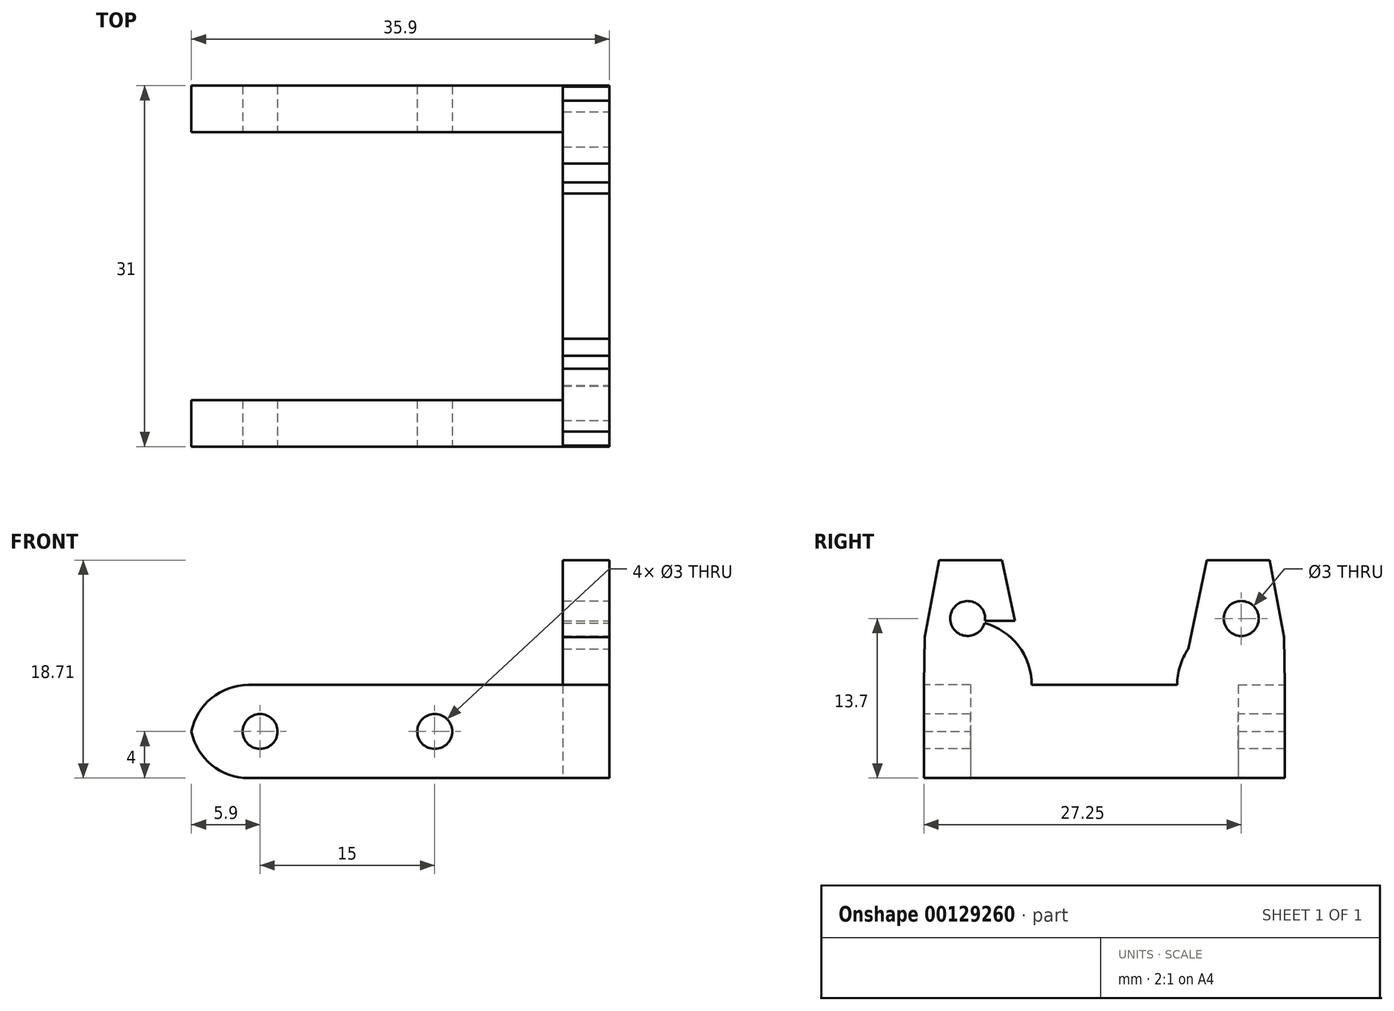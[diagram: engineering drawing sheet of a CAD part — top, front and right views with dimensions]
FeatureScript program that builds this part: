
annotation { "Feature Type Name" : "Feature", "Feature Type Description" : "" }
export const myFeature = defineFeature(function(context is Context, id is Id, definition is map)
    precondition{}
    {
        {
            var Q0;
            Q0=qCreatedBy(makeId("Top.planeOp"),FACE);
            var sketch = newSketch(context, id + "F0", { "sketchPlane" : qUnion([Q0])});
            skLineSegment(sketch, "E0", {"start": v(-25.25, 0) * mm, "end": v(21, 0) * mm, "construction": true});
            skLineSegment(sketch, "E1.0", {"start": v(-25.25, -11.5) * mm, "end": v(21, -11.5) * mm, "construction": true});
            skLineSegment(sketch, "E2", {"start": v(0, -19.54) * mm, "end": v(0, 24.09) * mm, "construction": true});
            skLineSegment(sketch, "E3.0", {"start": v(-18, -19.54) * mm, "end": v(-18, 24.09) * mm, "construction": true});
            skLineSegment(sketch, "E4.0", {"start": v(18, -19.54) * mm, "end": v(18, 24.09) * mm, "construction": true});
            skLineSegment(sketch, "E5.0", {"start": v(-12, -19.54) * mm, "end": v(-12, 24.09) * mm, "construction": true});
            skLineSegment(sketch, "E6.0", {"start": v(14, -19.54) * mm, "end": v(14, 24.09) * mm});
            skLineSegment(sketch, "E7", {"start": v(14, -11.5) * mm, "end": v(-18, -11.5) * mm});
            skLineSegment(sketch, "E8", {"start": v(-18, -11.5) * mm, "end": v(-18, -15.5) * mm});
            skLineSegment(sketch, "E9", {"start": v(-18, -15.5) * mm, "end": v(18, -15.5) * mm});
            skLineSegment(sketch, "E10", {"start": v(18, -15.5) * mm, "end": v(18, 0) * mm});
            skLineSegment(sketch, "E11.MirrorCS", {"start": v(-18, 15.5) * mm, "end": v(18, 15.5) * mm});
            skLineSegment(sketch, "E12.MirrorCS", {"start": v(14, 11.5) * mm, "end": v(-18, 11.5) * mm});
            skLineSegment(sketch, "E13.MirrorCS", {"start": v(-18, 11.5) * mm, "end": v(-18, 15.5) * mm});
            skLineSegment(sketch, "E14.MirrorCS", {"start": v(18, 15.5) * mm, "end": v(18, 0) * mm});
            skSolve(sketch);
        }
        {
            var Q0;
            {var subQ0=sQuery(id+"F0.wireOp",EDGE,"E12.MirrorCS");Q0=makeQuery(id+"F0.imprint","IMPRINT",FACE,{"disambiguationData":[TD([[makeQuery(id+"F0.imprint","IMPRINT",EDGE,{"derivedFrom":subQ0}),-1.0]])]});}
            var Q1;
            {var subQ0=sQuery(id+"F0.wireOp",EDGE,"E10");Q1=makeQuery(id+"F0.imprint","IMPRINT",FACE,{"disambiguationData":[TD([[makeQuery(id+"F0.imprint","IMPRINT",EDGE,{"derivedFrom":subQ0}),1.0]])]});}
            var Q2;
            {var subQ0=sQuery(id+"F0.wireOp",EDGE,"E7");Q2=makeQuery(id+"F0.imprint","IMPRINT",FACE,{"disambiguationData":[TD([[makeQuery(id+"F0.imprint","IMPRINT",EDGE,{"derivedFrom":subQ0}),1.0]])]});}
            extrude(context, id + "F1", {"entities" : qUnion([Q0, Q1, Q2]), "depth" : 8 * mm});
        }
        {
            var Q0;
            Q0=makeQuery(id+"F1.opExtrude","SWEPT_FACE",FACE,{"disambiguationData":[OSD([sQuery(id+"F0.wireOp",EDGE,"E10"),sQuery(id+"F0.wireOp",EDGE,"E14.MirrorCS")])]});
            var sketch = newSketch(context, id + "F2", { "sketchPlane" : qUnion([Q0])});
            skPoint(sketch, "E15.0", {"position": v(0, 0) * mm});
            skLineSegment(sketch, "E16.0", {"start": v(-15.5, 0) * mm, "end": v(15.5, 0) * mm, "construction": true});
            skLineSegment(sketch, "E17.0", {"start": v(-15.5, 8) * mm, "end": v(15.5, 8) * mm, "construction": true});
            skLineSegment(sketch, "E18", {"start": v(0, 0) * mm, "end": v(0, 8) * mm, "construction": true});
            skLineSegment(sketch, "E19.0", {"start": v(11.75, 0) * mm, "end": v(11.75, 8) * mm});
            skArc(sketch, "E20", {"start": v(15.42, 12.1) * mm, "mid": v(6.61, 9.97) * mm, "end": v(11.75, 2.5) * mm});
            skArc(sketch, "E21.MirrorC", {"start": v(-15.42, 12.1) * mm, "mid": v(-9.5, 13.02) * mm, "end": v(-6.25, 8) * mm});
            skLineSegment(sketch, "E22", {"start": v(11.75, 8) * mm, "end": v(11.75, 13.5) * mm, "construction": true});
            skLineSegment(sketch, "E23", {"start": v(11.75, 13.5) * mm, "end": v(-11.75, 13.5) * mm});
            skLineSegment(sketch, "E24.0", {"start": v(-13.75, 13.7) * mm, "end": v(13.75, 13.7) * mm, "construction": true});
            skCircle(sketch, "E25", {"center": v(11.75, 13.7) * mm, "radius": 1.5 * mm});
            skCircle(sketch, "E26.MirrorC", {"center": v(-11.75, 13.7) * mm, "radius": 1.5 * mm});
            skLineSegment(sketch, "E27", {"start": v(-15.42, 12.1) * mm, "end": v(-14.2, 18.71) * mm});
            skLineSegment(sketch, "E28", {"start": v(-14.2, 18.71) * mm, "end": v(-8.8, 18.71) * mm});
            skLineSegment(sketch, "E29", {"start": v(-8.8, 18.71) * mm, "end": v(-7.2, 11.09) * mm});
            skLineSegment(sketch, "E30.MirrorCS", {"start": v(8.8, 18.71) * mm, "end": v(7.2, 11.09) * mm});
            skLineSegment(sketch, "E31.MirrorCS", {"start": v(14.2, 18.71) * mm, "end": v(8.8, 18.71) * mm});
            skLineSegment(sketch, "E32.MirrorCS", {"start": v(15.42, 12.1) * mm, "end": v(14.2, 18.71) * mm});
            skLineSegment(sketch, "E33", {"start": v(-15.42, 12.1) * mm, "end": v(-15.5, 8) * mm});
            skLineSegment(sketch, "E34", {"start": v(15.42, 12.1) * mm, "end": v(15.5, 8) * mm});
            skSolve(sketch);
        }
        {
            var Q0;
            {var subQ0=sQuery(id+"F2.wireOp",EDGE,"E21.MirrorC");var subQ8=makeQuery(id+"F2.imprint","INTERSECT",VERTEX,{"derivedFrom":[subQ0,sQuery(id+"F2.wireOp",EDGE,"E27")]});Q0=makeQuery(id+"F2.imprint","IMPRINT",FACE,{"disambiguationData":[TD([[makeQuery(id+"F2.imprint","IMPRINT",EDGE,{"disambiguationData":[TD([[subQ8,-1.0]])],"derivedFrom":subQ0}),-1.0]])]});}
            var Q1;
            {var subQ0=sQuery(id+"F2.wireOp",EDGE,"E20");var subQ10=makeQuery(id+"F2.imprint","INTERSECT",VERTEX,{"derivedFrom":[subQ0,sQuery(id+"F2.wireOp",EDGE,"E32.MirrorCS")]});Q1=makeQuery(id+"F2.imprint","IMPRINT",FACE,{"disambiguationData":[TD([[makeQuery(id+"F2.imprint","IMPRINT",EDGE,{"disambiguationData":[TD([[subQ10,-1.0]])],"derivedFrom":subQ0}),1.0]])]});}
            var Q2;
            {var subQ8=sQuery(id+"F2.wireOp",EDGE,"E27");Q2=makeQuery(id+"F2.imprint","IMPRINT",FACE,{"disambiguationData":[TD([[makeQuery(id+"F2.imprint","IMPRINT",EDGE,{"derivedFrom":subQ8}),-1.0]])]});}
            var Q3;
            {var subQ0=sQuery(id+"F2.wireOp",EDGE,"E29");var subQ1=sQuery(id+"F2.wireOp",EDGE,"E21.MirrorC");var subQ2=makeQuery(id+"F2.imprint","INTERSECT",VERTEX,{"derivedFrom":[subQ1,subQ0]});Q3=makeQuery(id+"F2.imprint","IMPRINT",FACE,{"disambiguationData":[TD([[makeQuery(id+"F2.imprint","IMPRINT",EDGE,{"disambiguationData":[TD([[subQ2,1.0]])],"derivedFrom":subQ1}),1.0]])]});}
            var Q4;
            {var subQ0=sQuery(id+"F2.wireOp",EDGE,"E31.MirrorCS");Q4=makeQuery(id+"F2.imprint","IMPRINT",FACE,{"disambiguationData":[TD([[makeQuery(id+"F2.imprint","IMPRINT",EDGE,{"derivedFrom":subQ0}),1.0]])]});}
            var Q5;
            {var subQ0=sQuery(id+"F2.wireOp",EDGE,"E30.MirrorCS");var subQ1=sQuery(id+"F2.wireOp",EDGE,"E20");var subQ2=makeQuery(id+"F2.imprint","INTERSECT",VERTEX,{"derivedFrom":[subQ1,subQ0]});Q5=makeQuery(id+"F2.imprint","IMPRINT",FACE,{"disambiguationData":[TD([[makeQuery(id+"F2.imprint","IMPRINT",EDGE,{"disambiguationData":[TD([[subQ2,1.0]])],"derivedFrom":subQ1}),-1.0]])]});}
            var Q6;
            Q6=makeQuery(id+"F1.opExtrude","SWEPT_FACE",FACE,{"disambiguationData":[OSD([sQuery(id+"F0.wireOp",EDGE,"E6.0")])]});
            extrude(context, id + "F3", {"entities" : qUnion([Q0, Q1, Q2, Q3, Q4, Q5]), "operationType" : NewBodyOperationType.ADD, "endBound" : BoundingType.UP_TO_SURFACE, "oppositeDirection" : true, "endBoundEntityFace" : qUnion([Q6]), "depth" : 25 * mm});
        }
        {
            var Q0;
            Q0=makeQuery(id+"F2.imprint","IMPRINT",FACE,{"disambiguationData":[TD([[makeQuery(id+"F2.imprint","IMPRINT",EDGE,{"derivedFrom":sQuery(id+"F2.wireOp",EDGE,"E25")}),1.0]])]});
            var Q1;
            Q1=makeQuery(id+"F2.imprint","IMPRINT",FACE,{"disambiguationData":[TD([[makeQuery(id+"F2.imprint","IMPRINT",EDGE,{"derivedFrom":sQuery(id+"F2.wireOp",EDGE,"E26.MirrorC")}),-1.0]])]});
            extrude(context, id + "F4", {"entities" : qUnion([Q0, Q1]), "operationType" : NewBodyOperationType.REMOVE, "oppositeDirection" : true, "depth" : 25 * mm});
        }
        {
            var Q0;
            Q0=makeQuery(id+"F1.opExtrude","SWEPT_FACE",FACE,{"disambiguationData":[OSD([sQuery(id+"F0.wireOp",EDGE,"E9")])]});
            var sketch = newSketch(context, id + "F5", { "sketchPlane" : qUnion([Q0])});
            skLineSegment(sketch, "E35.0.0", {"start": v(14, 8) * mm, "end": v(14, 8) * mm});
            skLineSegment(sketch, "E35.0.1", {"start": v(14, 8) * mm, "end": v(14, 8) * mm});
            skLineSegment(sketch, "E35.0.2", {"start": v(-18, 8) * mm, "end": v(-18, 0) * mm});
            skLineSegment(sketch, "E35.0.3", {"start": v(-18, 0) * mm, "end": v(18, 0) * mm});
            skLineSegment(sketch, "E35.0.4", {"start": v(18, 0) * mm, "end": v(18, 8) * mm});
            skLineSegment(sketch, "E35.0.5", {"start": v(18, 8) * mm, "end": v(14, 8) * mm});
            skPoint(sketch, "E36.0", {"position": v(-12, 0) * mm});
            skLineSegment(sketch, "E37", {"start": v(-12, 0) * mm, "end": v(-12, 8) * mm, "construction": true});
            skLineSegment(sketch, "E38.0", {"start": v(3, 0) * mm, "end": v(3, 8) * mm, "construction": true});
            skCircle(sketch, "E39", {"center": v(-12, 4) * mm, "radius": 1.5 * mm});
            skCircle(sketch, "E40", {"center": v(3, 4) * mm, "radius": 1.5 * mm});
            skSolve(sketch);
        }
        {
            var Q0;
            Q0=makeQuery(id+"F5.imprint","IMPRINT",FACE,{"disambiguationData":[TD([[makeQuery(id+"F5.imprint","IMPRINT",EDGE,{"derivedFrom":sQuery(id+"F5.wireOp",EDGE,"E39")}),1.0]])]});
            var Q1;
            Q1=makeQuery(id+"F5.imprint","IMPRINT",FACE,{"disambiguationData":[TD([[makeQuery(id+"F5.imprint","IMPRINT",EDGE,{"derivedFrom":sQuery(id+"F5.wireOp",EDGE,"E40")}),1.0]])]});
            extrude(context, id + "F6", {"entities" : qUnion([Q0, Q1]), "operationType" : NewBodyOperationType.REMOVE, "oppositeDirection" : true, "depth" : 40 * mm});
        }
        {
            var Q0;
            Q0=makeQuery(id+"F1.opExtrude","CAP_EDGE",EDGE,{"disambiguationData":[OSD([sQuery(id+"F0.wireOp",EDGE,"E8")])],"isStart":false});
            var Q1;
            Q1=makeQuery(id+"F1.opExtrude","CAP_EDGE",EDGE,{"disambiguationData":[OSD([sQuery(id+"F0.wireOp",EDGE,"E13.MirrorCS")])],"isStart":false});
            var Q2;
            Q2=makeQuery(id+"F1.opExtrude","CAP_EDGE",EDGE,{"disambiguationData":[OSD([sQuery(id+"F0.wireOp",EDGE,"E8")])],"isStart":true});
            var Q3;
            Q3=makeQuery(id+"F1.opExtrude","CAP_EDGE",EDGE,{"disambiguationData":[OSD([sQuery(id+"F0.wireOp",EDGE,"E13.MirrorCS")])],"isStart":true});
            fillet(context, id + "F7", {"entities" : qUnion([Q0, Q1, Q2, Q3]), "radius" : 5 * mm, "tangentPropagation" : true, "allowEdgeOverflow" : false});
        }
    });
